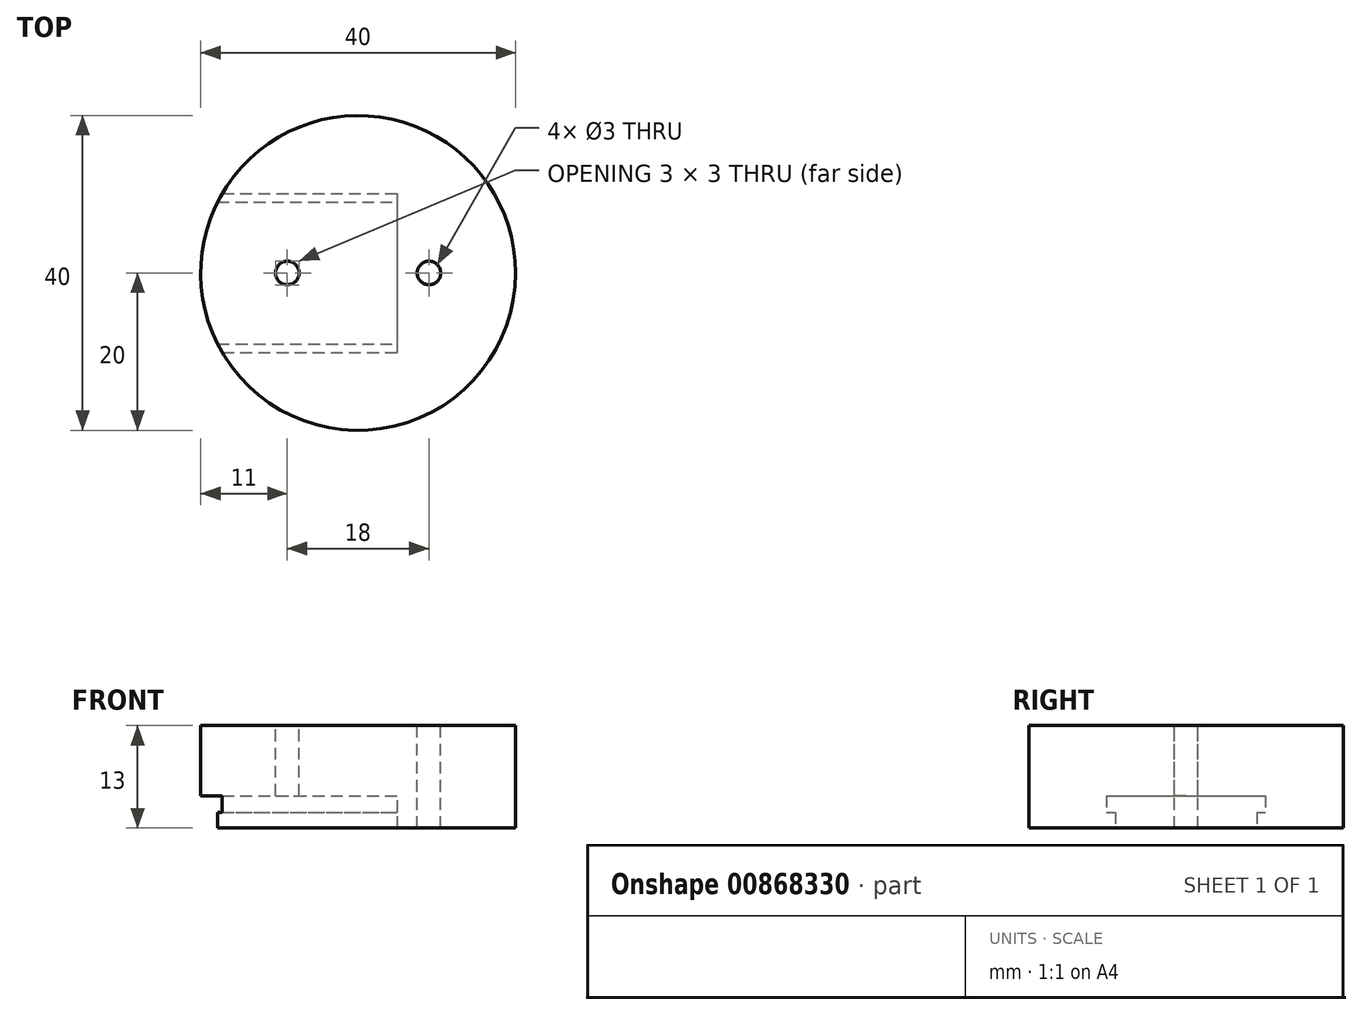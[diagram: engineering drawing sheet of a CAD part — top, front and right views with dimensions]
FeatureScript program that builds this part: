
annotation { "Feature Type Name" : "Feature", "Feature Type Description" : "" }
export const myFeature = defineFeature(function(context is Context, id is Id, definition is map)
    precondition{}
    {
        {
            var Q0;
            Q0=qCreatedBy(makeId("Top.planeOp"),FACE);
            var sketch = newSketch(context, id + "F0", { "sketchPlane" : qUnion([Q0])});
            skCircle(sketch, "E0", {"center": v(0, 0) * mm, "radius": 20 * mm});
            skSolve(sketch);
        }
        {
            var Q0;
            Q0=qSketchRegion(id+"F0",true);
            extrude(context, id + "F1", {"entities" : qUnion([Q0]), "depth" : 13 * mm, "offsetDistance" : 25 * mm});
        }
        {
            var Q0;
            Q0=qCreatedBy(makeId("Right.planeOp"),FACE);
            var sketch = newSketch(context, id + "F2", { "sketchPlane" : qUnion([Q0])});
            skLineSegment(sketch, "E1.bottom", {"start": v(-9, 0) * mm, "end": v(9, 0) * mm});
            skLineSegment(sketch, "E1.left", {"start": v(-9, 0) * mm, "end": v(-9, 2) * mm});
            skLineSegment(sketch, "E1.right", {"start": v(9, 0) * mm, "end": v(9, 2) * mm});
            skLineSegment(sketch, "E2.bottom", {"start": v(-10.1, 2) * mm, "end": v(-9, 2) * mm});
            skLineSegment(sketch, "E2.top", {"start": v(-10.1, 4.1) * mm, "end": v(10.1, 4.1) * mm});
            skLineSegment(sketch, "E2.left", {"start": v(-10.1, 2) * mm, "end": v(-10.1, 4.1) * mm});
            skLineSegment(sketch, "E2.right", {"start": v(10.1, 2) * mm, "end": v(10.1, 4.1) * mm});
            skLineSegment(sketch, "E3.trimOffspring", {"start": v(9, 2) * mm, "end": v(10.1, 2) * mm});
            skSolve(sketch);
        }
        {
            var Q0;
            Q0=qSketchRegion(id+"F2",true);
            extrude(context, id + "F3", {"entities" : qUnion([Q0]), "operationType" : NewBodyOperationType.REMOVE, "oppositeDirection" : true, "depth" : 25 * mm, "offsetDistance" : 25 * mm, "hasSecondDirection" : true, "secondDirectionOppositeDirection" : false, "secondDirectionDepth" : 5 * mm});
        }
        {
            var Q0;
            Q0=makeQuery(id+"F1.opExtrude","CAP_FACE",FACE,{"disambiguationData":[OSD([sQuery(id+"F0.wireOp",EDGE,"E0")])],"isStart":false});
            var sketch = newSketch(context, id + "F4", { "sketchPlane" : qUnion([Q0])});
            skCircle(sketch, "E4", {"center": v(-9, 0) * mm, "radius": 1.5 * mm});
            skCircle(sketch, "E5", {"center": v(9, 0) * mm, "radius": 1.5 * mm});
            skSolve(sketch);
        }
        {
            var Q0;
            Q0=qSketchRegion(id+"F4",true);
            extrude(context, id + "F5", {"entities" : qUnion([Q0]), "operationType" : NewBodyOperationType.REMOVE, "endBound" : BoundingType.THROUGH_ALL, "oppositeDirection" : true, "depth" : 25 * mm, "offsetDistance" : 25 * mm});
        }
    });
